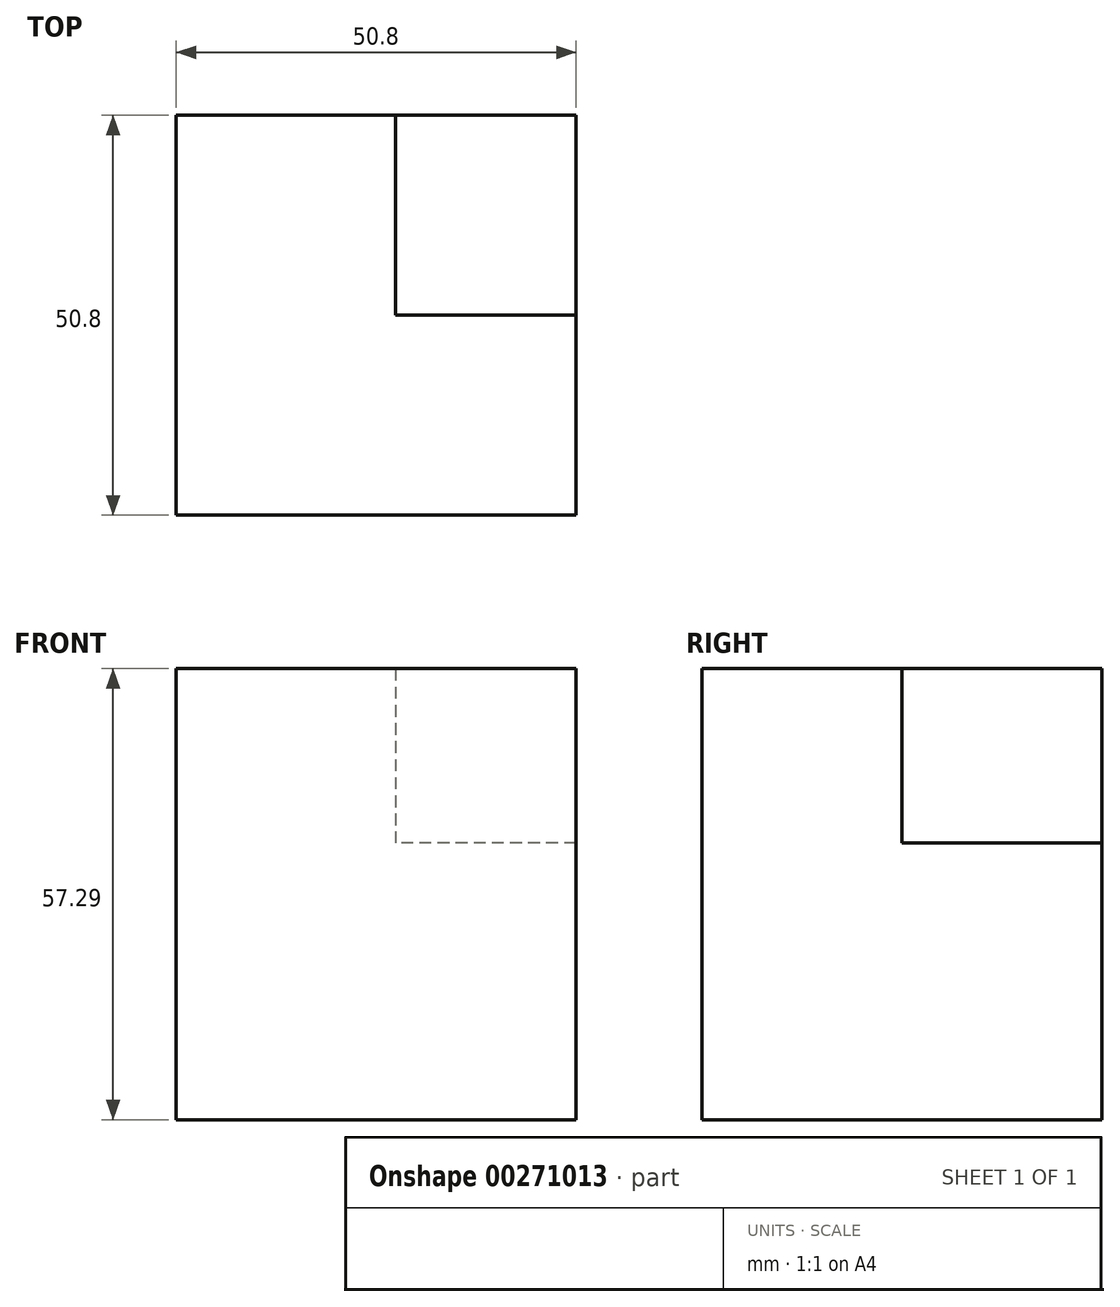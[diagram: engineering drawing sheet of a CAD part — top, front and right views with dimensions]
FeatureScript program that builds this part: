
annotation { "Feature Type Name" : "Feature", "Feature Type Description" : "" }
export const myFeature = defineFeature(function(context is Context, id is Id, definition is map)
    precondition{}
    {
        {
            var Q0;
            Q0=qCreatedBy(makeId("Front.planeOp"),FACE);
            var sketch = newSketch(context, id + "F0", { "sketchPlane" : qUnion([Q0])});
            skLineSegment(sketch, "E0", {"start": v(-50.8, 0) * mm, "end": v(-50.8, 57.29) * mm});
            skLineSegment(sketch, "E1", {"start": v(-50.8, 57.29) * mm, "end": v(0, 57.29) * mm});
            skLineSegment(sketch, "E2", {"start": v(0, 57.29) * mm, "end": v(0, 0) * mm});
            skLineSegment(sketch, "E3", {"start": v(0, 0) * mm, "end": v(-50.8, 0) * mm});
            skSolve(sketch);
        }
        {
            var Q0;
            Q0 = qSketchRegion(id + "F0", true);
            extrude(context, id + "F1", {"entities" : qUnion([Q0]), "depth" : 50.8 * mm});
        }
        {
            var Q0;
            Q0=makeQuery(id+"F1.opExtrude","CAP_FACE",FACE,{"disambiguationData":[OSD([sQuery(id+"F0.wireOp",EDGE,"E0"),sQuery(id+"F0.wireOp",EDGE,"E1"),sQuery(id+"F0.wireOp",EDGE,"E2"),sQuery(id+"F0.wireOp",EDGE,"E3")])],"isStart":true});
            var sketch = newSketch(context, id + "F2", { "sketchPlane" : qUnion([Q0])});
            skLineSegment(sketch, "E4.bottom", {"start": v(0, 57.29) * mm, "end": v(22.91, 57.29) * mm});
            skLineSegment(sketch, "E4.top", {"start": v(0, 35.14) * mm, "end": v(22.91, 35.14) * mm});
            skLineSegment(sketch, "E4.left", {"start": v(0, 57.29) * mm, "end": v(0, 35.14) * mm});
            skLineSegment(sketch, "E4.right", {"start": v(22.91, 57.29) * mm, "end": v(22.91, 35.14) * mm});
            skSolve(sketch);
        }
        {
            var Q0;
            Q0 = qSketchRegion(id + "F2", true);
            extrude(context, id + "F3", {"entities" : qUnion([Q0]), "operationType" : NewBodyOperationType.REMOVE, "oppositeDirection" : true, "depth" : 25.4 * mm});
        }
    });
